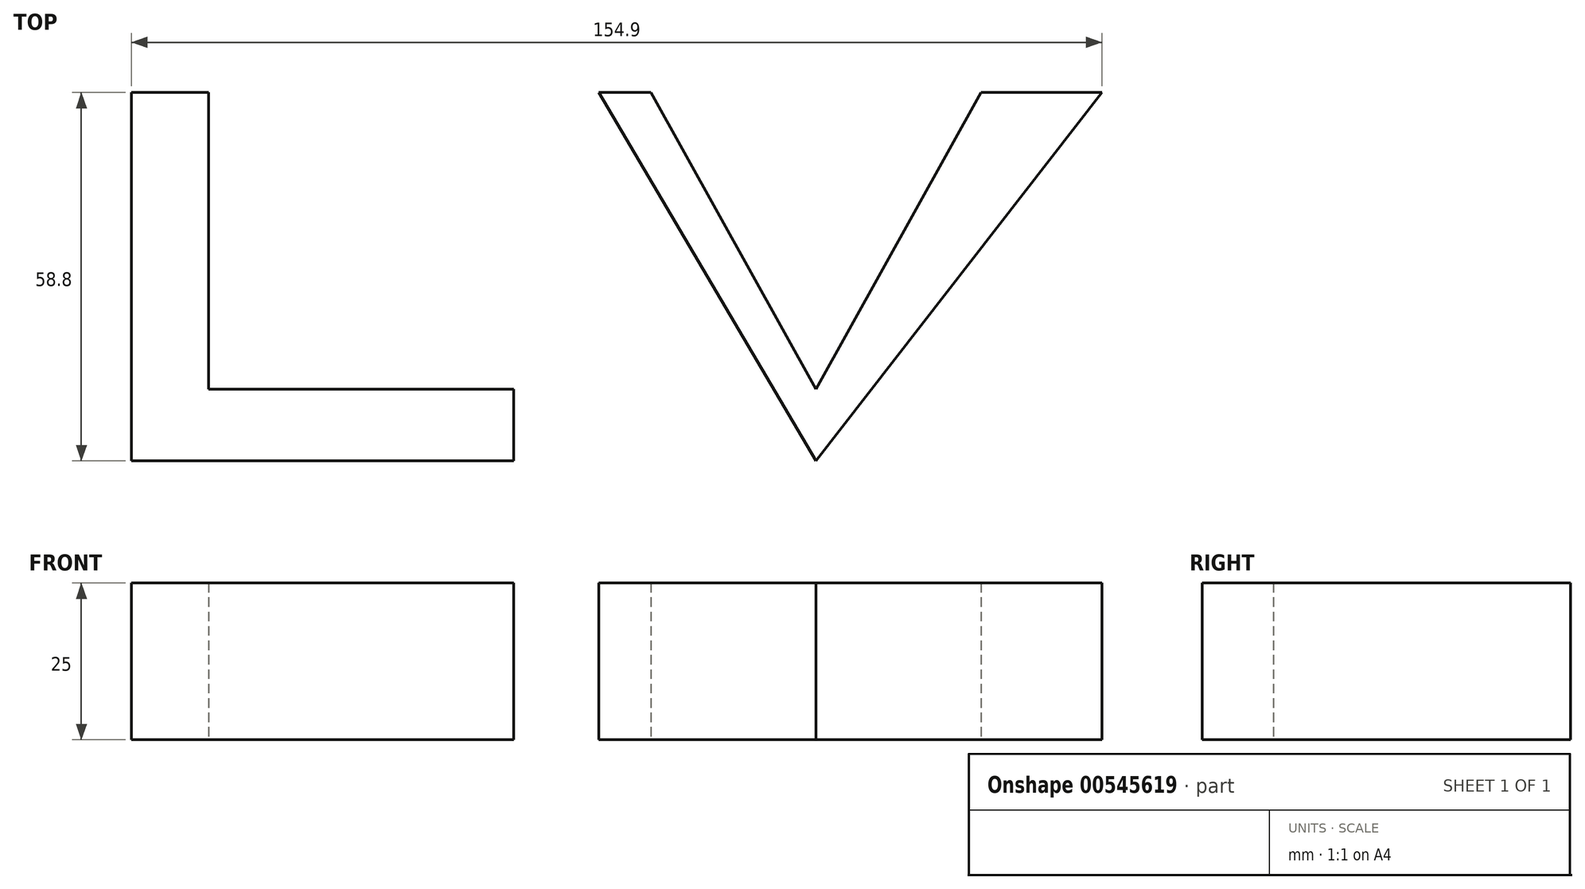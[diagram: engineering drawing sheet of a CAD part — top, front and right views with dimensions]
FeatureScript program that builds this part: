
annotation { "Feature Type Name" : "Feature", "Feature Type Description" : "" }
export const myFeature = defineFeature(function(context is Context, id is Id, definition is map)
    precondition{}
    {
        {
            var Q0;
            Q0=qCreatedBy(makeId("Top.planeOp"),FACE);
            var sketch = newSketch(context, id + "F0", { "sketchPlane" : qUnion([Q0])});
            skLineSegment(sketch, "E0", {"start": v(-98.3, 21.06) * mm, "end": v(-98.3, -37.74) * mm});
            skLineSegment(sketch, "E1", {"start": v(-98.3, -37.74) * mm, "end": v(-37.3, -37.74) * mm});
            skLineSegment(sketch, "E2", {"start": v(-37.3, -37.74) * mm, "end": v(-37.3, -26.33) * mm});
            skLineSegment(sketch, "E3", {"start": v(-37.3, -26.33) * mm, "end": v(-86, -26.33) * mm});
            skLineSegment(sketch, "E4", {"start": v(-86, -26.33) * mm, "end": v(-86, 21.06) * mm});
            skLineSegment(sketch, "E5", {"start": v(-86, 21.06) * mm, "end": v(-98.3, 21.06) * mm});
            skLineSegment(sketch, "E6", {"start": v(-23.7, 21.06) * mm, "end": v(10.97, -37.74) * mm});
            skPoint(sketch, "E6.startSnap0", {"position": v(-92.15, 21.06) * mm});
            skLineSegment(sketch, "E7", {"start": v(10.97, -37.74) * mm, "end": v(56.6, 21.06) * mm});
            skLineSegment(sketch, "E8", {"start": v(56.6, 21.06) * mm, "end": v(37.3, 21.06) * mm});
            skLineSegment(sketch, "E9", {"start": v(37.3, 21.06) * mm, "end": v(10.97, -26.33) * mm});
            skLineSegment(sketch, "E10", {"start": v(10.97, -26.33) * mm, "end": v(-15.36, 21.06) * mm});
            skLineSegment(sketch, "E11", {"start": v(-15.36, 21.06) * mm, "end": v(-23.7, 21.06) * mm});
            skSolve(sketch);
        }
        {
            var Q0;
            Q0 = qSketchRegion(id + "F0", true);
            extrude(context, id + "F1", {"entities" : qUnion([Q0]), "depth" : 25 * mm, "offsetDistance" : 25 * mm});
        }
    });
